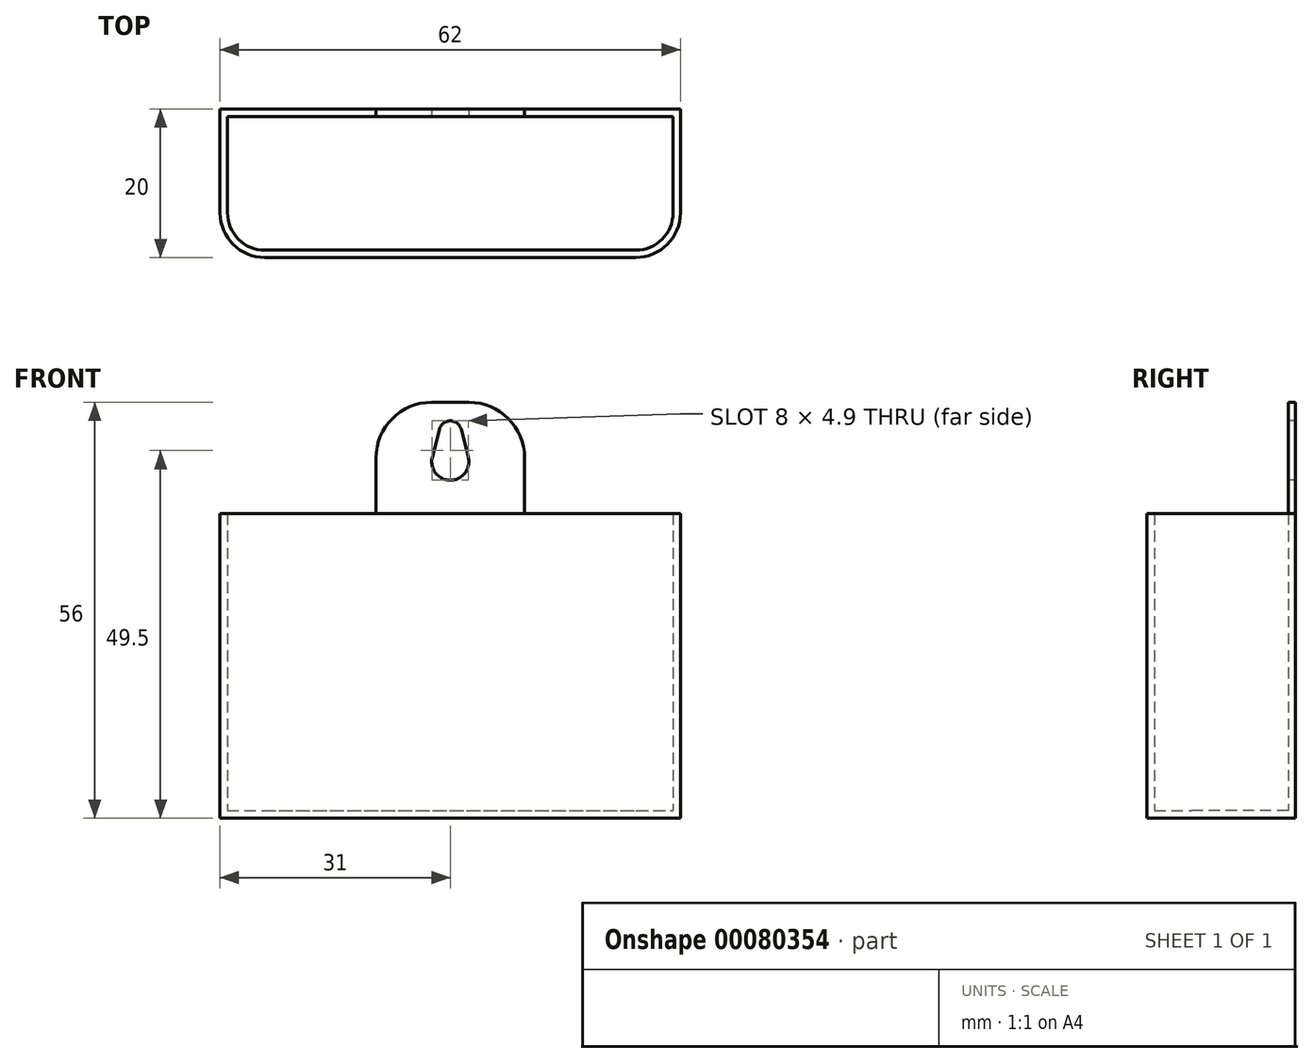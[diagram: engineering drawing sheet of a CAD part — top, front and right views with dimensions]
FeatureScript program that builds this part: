
annotation { "Feature Type Name" : "Feature", "Feature Type Description" : "" }
export const myFeature = defineFeature(function(context is Context, id is Id, definition is map)
    precondition{}
    {
        {
            var Q0;
            Q0=qCreatedBy(makeId("Top.planeOp"),FACE);
            var sketch = newSketch(context, id + "F0", { "sketchPlane" : qUnion([Q0])});
            skLineSegment(sketch, "E0.bottom", {"start": v(0, 0) * mm, "end": v(62, 0) * mm});
            skLineSegment(sketch, "E0.top", {"start": v(0, 20) * mm, "end": v(62, 20) * mm});
            skLineSegment(sketch, "E0.left", {"start": v(0, 0) * mm, "end": v(0, 20) * mm});
            skLineSegment(sketch, "E0.right", {"start": v(62, 0) * mm, "end": v(62, 20) * mm});
            skSolve(sketch);
        }
        {
            var Q0;
            Q0 = qSketchRegion(id + "F0", true);
            extrude(context, id + "F1", {"entities" : qUnion([Q0]), "depth" : 1 * mm});
        }
        {
            var Q0;
            Q0=makeQuery(id+"F1.opExtrude","CAP_FACE",FACE,{"disambiguationData":[OSD([sQuery(id+"F0.wireOp",EDGE,"E0.bottom"),sQuery(id+"F0.wireOp",EDGE,"E0.top"),sQuery(id+"F0.wireOp",EDGE,"E0.left"),sQuery(id+"F0.wireOp",EDGE,"E0.right")])],"isStart":false});
            var sketch = newSketch(context, id + "F2", { "sketchPlane" : qUnion([Q0])});
            skLineSegment(sketch, "E1.bottom", {"start": v(0, 20) * mm, "end": v(62, 20) * mm});
            skLineSegment(sketch, "E1.top", {"start": v(0, 0) * mm, "end": v(62, 0) * mm});
            skLineSegment(sketch, "E1.left", {"start": v(0, 20) * mm, "end": v(0, 0) * mm});
            skLineSegment(sketch, "E1.right", {"start": v(62, 20) * mm, "end": v(62, 0) * mm});
            skLineSegment(sketch, "E2.0", {"start": v(1, 19) * mm, "end": v(61, 19) * mm});
            skLineSegment(sketch, "E2.1", {"start": v(1, 19) * mm, "end": v(1, 1) * mm});
            skLineSegment(sketch, "E2.2", {"start": v(1, 1) * mm, "end": v(61, 1) * mm});
            skLineSegment(sketch, "E2.3", {"start": v(61, 19) * mm, "end": v(61, 1) * mm});
            skSolve(sketch);
        }
        {
            var Q0;
            Q0 = qSketchRegion(id + "F2", true);
            extrude(context, id + "F3", {"entities" : qUnion([Q0]), "operationType" : NewBodyOperationType.ADD, "depth" : 40 * mm});
        }
        {
            var Q0;
            Q0=makeQuery(id+"F3.opExtrude","SWEPT_EDGE",EDGE,{"disambiguationData":[OSD([sQuery(id+"F2.wireOp",EDGE,"E2.1"),sQuery(id+"F2.wireOp",EDGE,"E2.2")])]});
            var Q1;
            Q1=makeQuery(id+"F3.opExtrude","SWEPT_EDGE",EDGE,{"disambiguationData":[OSD([sQuery(id+"F2.wireOp",EDGE,"E2.2"),sQuery(id+"F2.wireOp",EDGE,"E2.3")])]});
            fillet(context, id + "F4", {"entities" : qUnion([Q0, Q1]), "radius" : 5 * mm, "tangentPropagation" : true, "allowEdgeOverflow" : false});
        }
        {
            var Q0;
            Q0=makeQuery(id+"F3.boolean.opBoolean","MERGE",EDGE,{"derivedFrom":[makeQuery(id+"F1.opExtrude","SWEPT_EDGE",EDGE,{"disambiguationData":[OSD([sQuery(id+"F0.wireOp",EDGE,"E0.bottom"),sQuery(id+"F0.wireOp",EDGE,"E0.left")])]}),makeQuery(id+"F3.opExtrude","SWEPT_EDGE",EDGE,{"disambiguationData":[OSD([sQuery(id+"F2.wireOp",EDGE,"E1.top"),sQuery(id+"F2.wireOp",EDGE,"E1.left")])]})]});
            var Q1;
            Q1=makeQuery(id+"F3.boolean.opBoolean","MERGE",EDGE,{"derivedFrom":[makeQuery(id+"F1.opExtrude","SWEPT_EDGE",EDGE,{"disambiguationData":[OSD([sQuery(id+"F0.wireOp",EDGE,"E0.bottom"),sQuery(id+"F0.wireOp",EDGE,"E0.right")])]}),makeQuery(id+"F3.opExtrude","SWEPT_EDGE",EDGE,{"disambiguationData":[OSD([sQuery(id+"F2.wireOp",EDGE,"E1.top"),sQuery(id+"F2.wireOp",EDGE,"E1.right")])]})]});
            fillet(context, id + "F5", {"entities" : qUnion([Q0, Q1]), "radius" : 6 * mm, "tangentPropagation" : true, "allowEdgeOverflow" : false});
        }
        {
            var Q0;
            Q0=makeQuery(id+"F3.opExtrude","CAP_FACE",FACE,{"disambiguationData":[OSD([sQuery(id+"F2.wireOp",EDGE,"E1.bottom"),sQuery(id+"F2.wireOp",EDGE,"E1.top"),sQuery(id+"F2.wireOp",EDGE,"E1.left"),sQuery(id+"F2.wireOp",EDGE,"E1.right"),sQuery(id+"F2.wireOp",EDGE,"E2.0"),sQuery(id+"F2.wireOp",EDGE,"E2.1"),sQuery(id+"F2.wireOp",EDGE,"E2.2"),sQuery(id+"F2.wireOp",EDGE,"E2.3")])],"isStart":false});
            var sketch = newSketch(context, id + "F6", { "sketchPlane" : qUnion([Q0])});
            skLineSegment(sketch, "E3.bottom", {"start": v(21, 20) * mm, "end": v(41, 20) * mm});
            skLineSegment(sketch, "E3.top", {"start": v(21, 19) * mm, "end": v(41, 19) * mm});
            skLineSegment(sketch, "E3.left", {"start": v(21, 20) * mm, "end": v(21, 19) * mm});
            skLineSegment(sketch, "E3.right", {"start": v(41, 20) * mm, "end": v(41, 19) * mm});
            skSolve(sketch);
        }
        {
            var Q0;
            Q0 = qSketchRegion(id + "F6", true);
            extrude(context, id + "F7", {"entities" : qUnion([Q0]), "operationType" : NewBodyOperationType.ADD, "depth" : 15 * mm});
        }
        {
            var Q0;
            Q0=makeQuery(id+"F7.boolean.opBoolean","MERGE",FACE,{"derivedFrom":[makeQuery(id+"F3.opExtrude","SWEPT_FACE",FACE,{"disambiguationData":[OSD([sQuery(id+"F2.wireOp",EDGE,"E2.0")])]}),makeQuery(id+"F7.opExtrude","SWEPT_FACE",FACE,{"disambiguationData":[OSD([sQuery(id+"F6.wireOp",EDGE,"E3.top")])]})]});
            var sketch = newSketch(context, id + "F8", { "sketchPlane" : qUnion([Q0])});
            skLineSegment(sketch, "E4", {"start": v(31, 41) * mm, "end": v(31, 56) * mm, "construction": true});
            skPoint(sketch, "E4.startSnap0", {"position": v(31, 56) * mm});
            skArc(sketch, "E5", {"start": v(32.45, 52.38) * mm, "mid": v(31, 53.5) * mm, "end": v(29.55, 52.38) * mm});
            skArc(sketch, "E6", {"start": v(28.58, 48.62) * mm, "mid": v(31, 45.5) * mm, "end": v(33.42, 48.62) * mm});
            skLineSegment(sketch, "E7", {"start": v(29.55, 52.38) * mm, "end": v(28.58, 48.62) * mm});
            skLineSegment(sketch, "E8", {"start": v(32.45, 52.38) * mm, "end": v(33.42, 48.62) * mm});
            skSolve(sketch);
        }
        {
            var Q0;
            Q0 = qSketchRegion(id + "F8", true);
            var Q1;
            Q1=makeQuery(id+"F7.boolean.opBoolean","MERGE",FACE,{"derivedFrom":[makeQuery(id+"F3.boolean.opBoolean","MERGE",FACE,{"derivedFrom":[makeQuery(id+"F1.opExtrude","SWEPT_FACE",FACE,{"disambiguationData":[OSD([sQuery(id+"F0.wireOp",EDGE,"E0.top")])]}),makeQuery(id+"F3.opExtrude","SWEPT_FACE",FACE,{"disambiguationData":[OSD([sQuery(id+"F2.wireOp",EDGE,"E1.bottom")])]})]}),makeQuery(id+"F7.opExtrude","SWEPT_FACE",FACE,{"disambiguationData":[OSD([sQuery(id+"F6.wireOp",EDGE,"E3.bottom")])]})]});
            extrude(context, id + "F9", {"entities" : qUnion([Q0]), "operationType" : NewBodyOperationType.REMOVE, "endBound" : BoundingType.UP_TO_SURFACE, "oppositeDirection" : true, "endBoundEntityFace" : qUnion([Q1]), "depth" : 25 * mm});
        }
        {
            var Q0;
            Q0=makeQuery(id+"F7.opExtrude","CAP_EDGE",EDGE,{"disambiguationData":[OSD([sQuery(id+"F6.wireOp",EDGE,"E3.left")])],"isStart":false});
            var Q1;
            Q1=makeQuery(id+"F7.opExtrude","CAP_EDGE",EDGE,{"disambiguationData":[OSD([sQuery(id+"F6.wireOp",EDGE,"E3.right")])],"isStart":false});
            var Q2;
            Q2=makeQuery(id+"F7.opExtrude","CAP_EDGE",EDGE,{"disambiguationData":[OSD([sQuery(id+"F6.wireOp",EDGE,"E3.right")])],"isStart":true});
            var Q3;
            Q3=makeQuery(id+"F7.opExtrude","CAP_EDGE",EDGE,{"disambiguationData":[OSD([sQuery(id+"F6.wireOp",EDGE,"E3.left")])],"isStart":true});
            fillet(context, id + "F10", {"entities" : qUnion([Q0, Q1, Q2, Q3]), "radius" : 7.5 * mm, "tangentPropagation" : true, "allowEdgeOverflow" : false});
        }
    });
